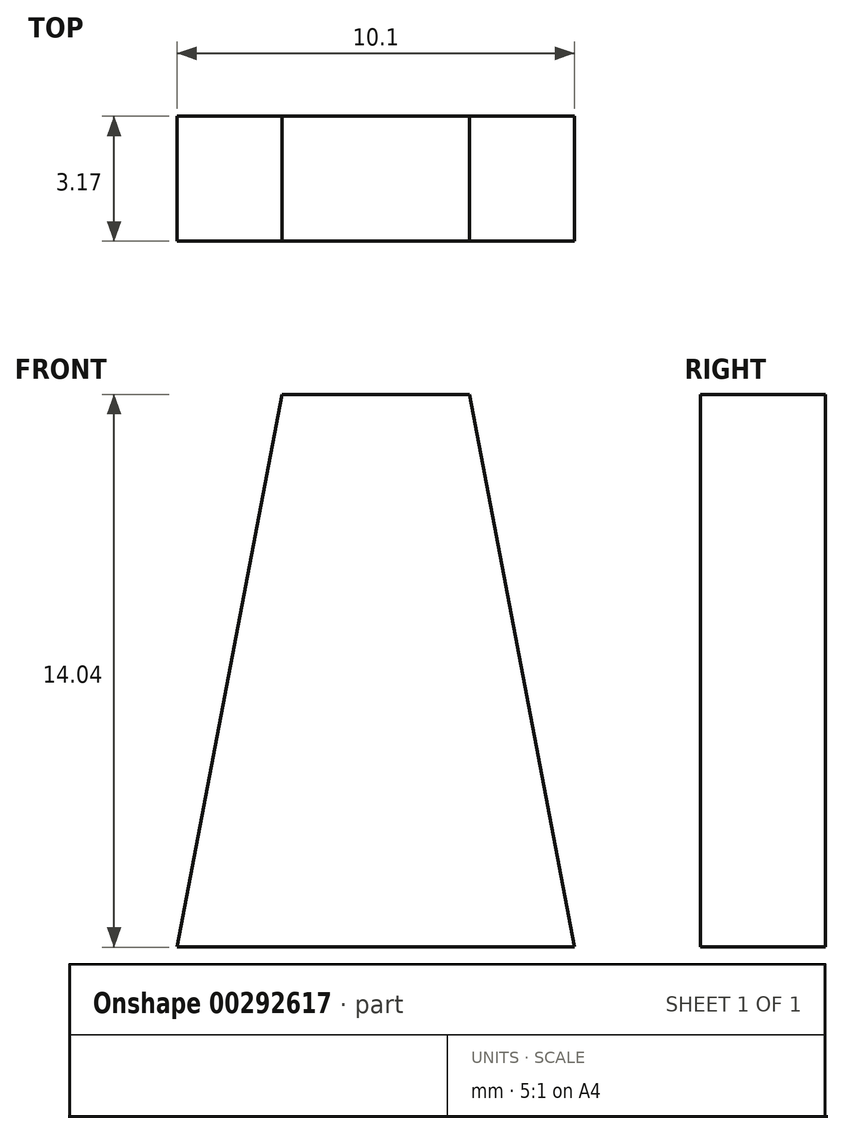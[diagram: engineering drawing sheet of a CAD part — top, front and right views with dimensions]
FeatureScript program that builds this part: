
annotation { "Feature Type Name" : "Feature", "Feature Type Description" : "" }
export const myFeature = defineFeature(function(context is Context, id is Id, definition is map)
    precondition{}
    {
        {
            var Q0;
            Q0=qCreatedBy(makeId("Front.planeOp"),FACE);
            var sketch = newSketch(context, id + "F0", { "sketchPlane" : qUnion([Q0])});
            skLineSegment(sketch, "E0.bottom", {"start": v(-4.76, 4.76) * mm, "end": v(4.76, 4.76) * mm});
            skLineSegment(sketch, "E0.top", {"start": v(-4.76, -4.76) * mm, "end": v(4.76, -4.76) * mm});
            skLineSegment(sketch, "E0.left", {"start": v(-4.76, 4.76) * mm, "end": v(-4.76, -4.76) * mm});
            skLineSegment(sketch, "E0.right", {"start": v(4.76, 4.76) * mm, "end": v(4.76, -4.76) * mm});
            skPoint(sketch, "E0.middle", {"position": v(0, 0) * mm});
            skSolve(sketch);
        }
        {
            var Q0;
            Q0=qCreatedBy(makeId("Front.planeOp"),FACE);
            var sketch = newSketch(context, id + "F1", { "sketchPlane" : qUnion([Q0])});
            skLineSegment(sketch, "E1", {"start": v(4.86, 5.58) * mm, "end": v(2.2, 19.62) * mm});
            skLineSegment(sketch, "E2", {"start": v(2.2, 19.62) * mm, "end": v(-2.57, 19.62) * mm});
            skLineSegment(sketch, "E3", {"start": v(-2.57, 19.62) * mm, "end": v(-5.24, 5.58) * mm});
            skLineSegment(sketch, "E4", {"start": v(-5.24, 5.58) * mm, "end": v(4.86, 5.58) * mm});
            skSolve(sketch);
        }
        {
            var Q0;
            Q0=makeQuery(id+"F1.imprint","IMPRINT",FACE,{"disambiguationData":[TD([[makeQuery(id+"F1.imprint","IMPRINT",EDGE,{"derivedFrom":sQuery(id+"F1.wireOp",EDGE,"E1")}),1.0]])]});
            extrude(context, id + "F2", {"entities" : qUnion([Q0]), "oppositeDirection" : true, "depth" : 3.17 * mm});
        }
    });
